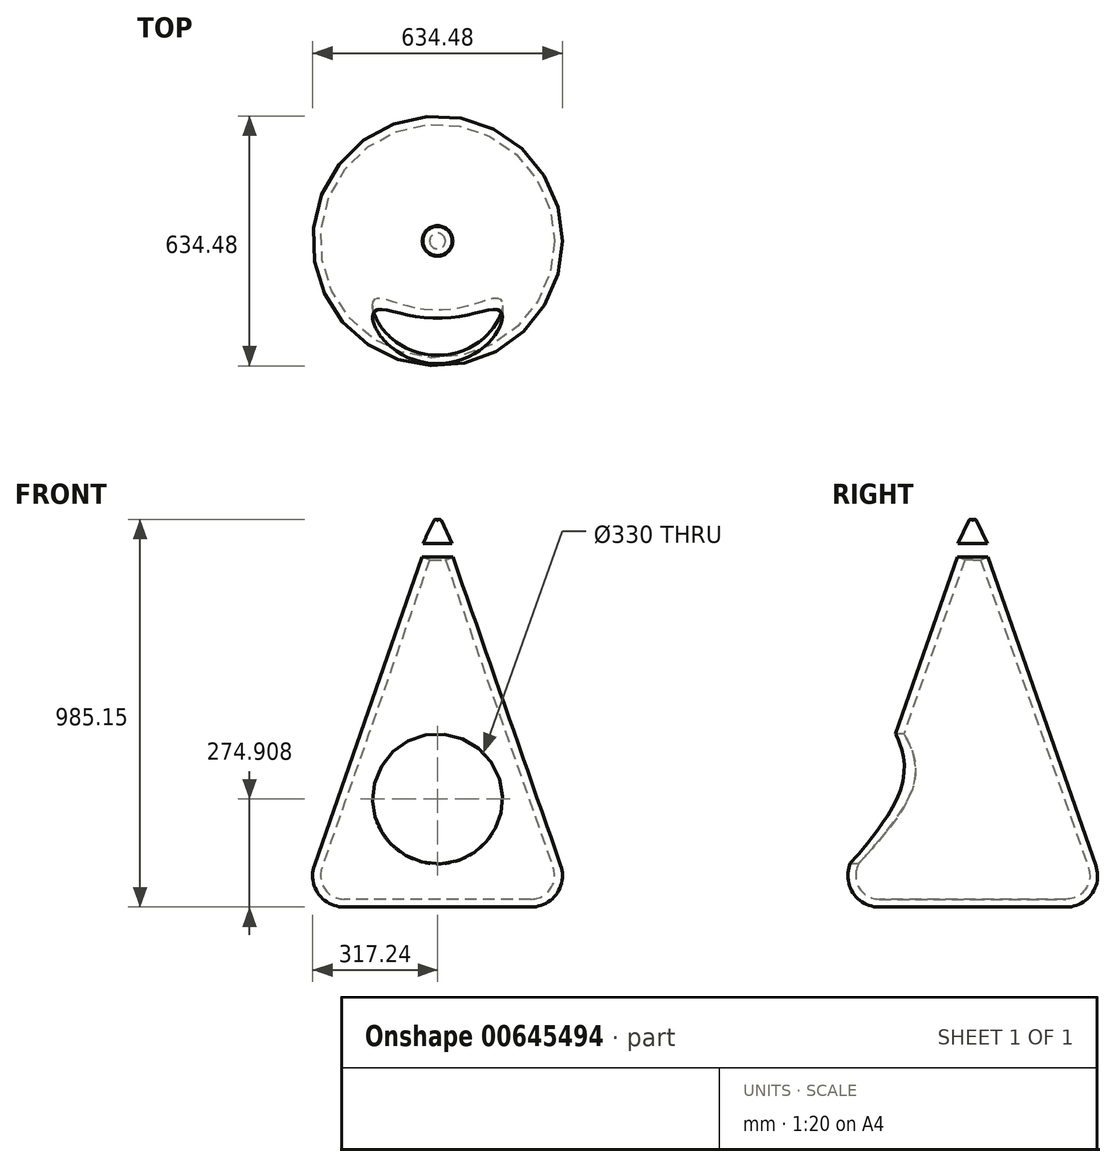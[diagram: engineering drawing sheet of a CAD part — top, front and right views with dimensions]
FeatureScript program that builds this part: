
annotation { "Feature Type Name" : "Feature", "Feature Type Description" : "" }
export const myFeature = defineFeature(function(context is Context, id is Id, definition is map)
    precondition{}
    {
        {
            var Q0;
            Q0=qCreatedBy(makeId("Front.planeOp"),FACE);
            var sketch = newSketch(context, id + "F0", { "sketchPlane" : qUnion([Q0])});
            skLineSegment(sketch, "E0", {"start": v(0, 552.3) * mm, "end": v(0, -330.02) * mm});
            skLineSegment(sketch, "E1", {"start": v(0, -330.02) * mm, "end": v(-237.24, -330.02) * mm});
            skLineSegment(sketch, "E2", {"start": v(-312.75, -223.6) * mm, "end": v(-38.88, 558.9) * mm});
            skPoint(sketch, "E3.visualSharp", {"position": v(-350, -330.02) * mm});
            skArc(sketch, "E3.filletArc", {"start": v(-312.75, -223.6) * mm, "mid": v(-302.49, -296.3) * mm, "end": v(-237.24, -330.02) * mm});
            skPoint(sketch, "E4.visualSharp", {"position": v(0, 669.98) * mm});
            skArc(sketch, "E4.filletArc", {"start": v(0, 552.3) * mm, "mid": v(-16.65, 572.01) * mm, "end": v(-38.88, 558.9) * mm});
            skSolve(sketch);
        }
        {
            var Q0;
            Q0=makeQuery(id+"F0.imprint","IMPRINT",FACE,{"disambiguationData":[TD([[makeQuery(id+"F0.imprint","IMPRINT",EDGE,{"derivedFrom":sQuery(id+"F0.wireOp",EDGE,"E0")}),-1.0]])]});
            var Q1;
            Q1=sQuery(id+"F0.wireOp",EDGE,"E0");
            revolve(context, id + "F1", {"entities" : qUnion([Q0]), "axis" : qUnion([Q1]), "revolveType" : RevolveType.FULL});
        }
        {
            var Q0;
            Q0=makeQuery(id+"F1.opRevolve","SWEPT_FACE",FACE,{"disambiguationData":[OSD([sQuery(id+"F0.wireOp",EDGE,"E4.filletArc")])]});
            var Q1;
            Q1=makeQuery(id+"F1.opRevolve","SWEPT_BODY",BODY,{"disambiguationData":[OSD([sQuery(id+"F0.wireOp",EDGE,"E0"),sQuery(id+"F0.wireOp",EDGE,"E1"),sQuery(id+"F0.wireOp",EDGE,"E2"),sQuery(id+"F0.wireOp",EDGE,"E3.filletArc"),sQuery(id+"F0.wireOp",EDGE,"E4.filletArc")])]});
            shell(context, id + "F2", {"entities" : qUnion([Q0]), "parts" : qUnion([Q1]), "thickness" : 20 * mm});
        }
        {
            var Q0;
            Q0=qCreatedBy(makeId("Front.planeOp"),FACE);
            cPlane(context, id + "F3", {"entities" : qUnion([Q0]), "cplaneType" : CPlaneType.OFFSET, "offset" : 447 * mm, "width" : 150 * mm, "height" : 150 * mm});
        }
        {
            var Q0;
            Q0=qCreatedBy(id+"F3.planeOp",FACE);
            var sketch = newSketch(context, id + "F4", { "sketchPlane" : qUnion([Q0])});
            skCircle(sketch, "E5", {"center": v(0, -55.11) * mm, "radius": 165 * mm});
            skSolve(sketch);
        }
        {
            var Q0;
            Q0=makeQuery(id+"F4.imprint","IMPRINT",FACE,{"disambiguationData":[TD([[makeQuery(id+"F4.imprint","IMPRINT",EDGE,{"derivedFrom":sQuery(id+"F4.wireOp",EDGE,"E5")}),1.0]])]});
            extrude(context, id + "F5", {"entities" : qUnion([Q0]), "operationType" : NewBodyOperationType.REMOVE, "oppositeDirection" : true, "depth" : 506 * mm, "offsetDistance" : 25 * mm});
        }
        {
            var Q0;
            Q0=qCreatedBy(makeId("Front.planeOp"),FACE);
            var sketch = newSketch(context, id + "F6", { "sketchPlane" : qUnion([Q0])});
            skLineSegment(sketch, "E6", {"start": v(0, 594.65) * mm, "end": v(0, 650.13) * mm});
            skLineSegment(sketch, "E7", {"start": v(-37, 594.22) * mm, "end": v(-9.52, 652.27) * mm});
            skLineSegment(sketch, "E8", {"start": v(-37, 594.22) * mm, "end": v(0, 594.65) * mm});
            skPoint(sketch, "E9.visualSharp", {"position": v(0, 672.38) * mm});
            skArc(sketch, "E9.filletArc", {"start": v(0, 650.13) * mm, "mid": v(-3.9, 655.01) * mm, "end": v(-9.52, 652.27) * mm});
            skSolve(sketch);
        }
        {
            var Q0;
            {var subQ2=sQuery(id+"F6.wireOp",EDGE,"E7");Q0=makeQuery(id+"F6.imprint","IMPRINT",FACE,{"disambiguationData":[TD([[makeQuery(id+"F6.imprint","IMPRINT",EDGE,{"derivedFrom":subQ2}),-1.0]])]});}
            var Q1;
            Q1=sQuery(id+"F6.wireOp",EDGE,"E6");
            revolve(context, id + "F7", {"entities" : qUnion([Q0]), "axis" : qUnion([Q1]), "revolveType" : RevolveType.FULL});
        }
    });
